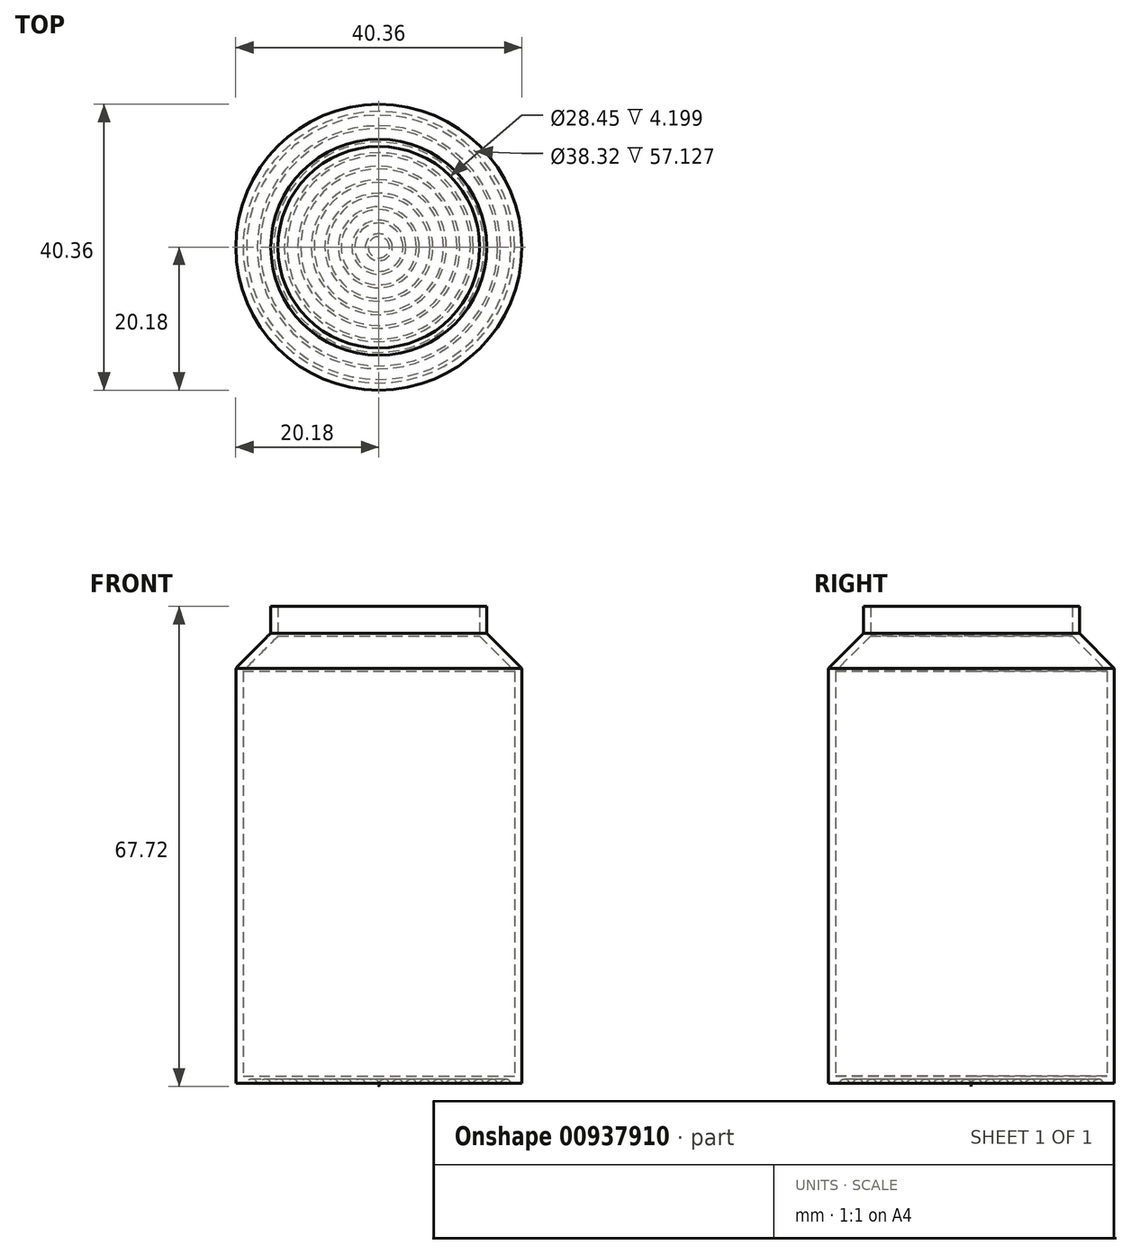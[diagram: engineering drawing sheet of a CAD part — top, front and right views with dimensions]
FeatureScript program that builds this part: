
annotation { "Feature Type Name" : "Feature", "Feature Type Description" : "" }
export const myFeature = defineFeature(function(context is Context, id is Id, definition is map)
    precondition{}
    {
        {
            var Q0;
            Q0=qCreatedBy(makeId("Front.planeOp"),FACE);
            var sketch = newSketch(context, id + "F0", { "sketchPlane" : qUnion([Q0])});
            skLineSegment(sketch, "E0", {"start": v(0, 0) * mm, "end": v(0, 99.8) * mm});
            skLineSegment(sketch, "E1", {"start": v(15.24, 0) * mm, "end": v(14.84, 0) * mm});
            skLineSegment(sketch, "E2", {"start": v(15.24, 67.3) * mm, "end": v(15.24, 63.52) * mm});
            skLineSegment(sketch, "E3", {"start": v(15.24, 63.52) * mm, "end": v(20.18, 58.56) * mm});
            skLineSegment(sketch, "E4", {"start": v(20.18, 58.56) * mm, "end": v(20.18, 0) * mm});
            skLineSegment(sketch, "E5", {"start": v(20.18, 0) * mm, "end": v(18.65, 0) * mm});
            skLineSegment(sketch, "E6.0", {"start": v(15.24, 1.02) * mm, "end": v(0, 1.02) * mm});
            skLineSegment(sketch, "E6.1", {"start": v(14.22, 67.3) * mm, "end": v(14.22, 63.1) * mm});
            skLineSegment(sketch, "E6.2", {"start": v(14.22, 63.1) * mm, "end": v(19.16, 58.14) * mm});
            skLineSegment(sketch, "E6.3", {"start": v(19.16, 58.14) * mm, "end": v(19.16, 1.02) * mm});
            skLineSegment(sketch, "E6.4", {"start": v(19.16, 1.02) * mm, "end": v(15.24, 1.02) * mm});
            skLineSegment(sketch, "E7", {"start": v(14.22, 67.3) * mm, "end": v(15.24, 67.3) * mm});
            skArc(sketch, "E8", {"start": v(1.5, 0) * mm, "mid": v(0.75, 0.57) * mm, "end": v(0, 0) * mm});
            skArc(sketch, "E9.1.0.0", {"start": v(3.4, 0) * mm, "mid": v(2.66, 0.57) * mm, "end": v(1.9, 0) * mm});
            skArc(sketch, "E9.2.0.0", {"start": v(5.31, 0) * mm, "mid": v(4.56, 0.57) * mm, "end": v(3.81, 0) * mm});
            skArc(sketch, "E9.3.0.0", {"start": v(7.22, 0) * mm, "mid": v(6.47, 0.57) * mm, "end": v(5.71, 0) * mm});
            skArc(sketch, "E9.4.0.0", {"start": v(9.12, 0) * mm, "mid": v(8.37, 0.57) * mm, "end": v(7.62, 0) * mm});
            skArc(sketch, "E9.5.0.0", {"start": v(11.03, 0) * mm, "mid": v(10.28, 0.57) * mm, "end": v(9.53, 0) * mm});
            skArc(sketch, "E9.6.0.0", {"start": v(12.93, 0) * mm, "mid": v(12.18, 0.57) * mm, "end": v(11.43, 0) * mm});
            skArc(sketch, "E9.7.0.0", {"start": v(14.84, 0) * mm, "mid": v(14.09, 0.57) * mm, "end": v(13.33, 0) * mm});
            skArc(sketch, "E9.8.0.0", {"start": v(16.74, 0) * mm, "mid": v(16, 0.57) * mm, "end": v(15.24, 0) * mm});
            skArc(sketch, "E9.9.0.0", {"start": v(18.65, 0) * mm, "mid": v(17.9, 0.57) * mm, "end": v(17.14, 0) * mm});
            skLineSegment(sketch, "E9.direction1", {"start": v(1.5, 0) * mm, "end": v(1.9, 0) * mm, "construction": true});
            skLineSegment(sketch, "E10.trimOffspring", {"start": v(5.71, 0) * mm, "end": v(5.31, 0) * mm});
            skLineSegment(sketch, "E11.trimOffspring", {"start": v(3.81, 0) * mm, "end": v(3.4, 0) * mm});
            skLineSegment(sketch, "E12.trimOffspring", {"start": v(1.9, 0) * mm, "end": v(1.5, 0) * mm});
            skLineSegment(sketch, "E13.trimOffspring", {"start": v(7.62, 0) * mm, "end": v(7.22, 0) * mm});
            skLineSegment(sketch, "E14.trimOffspring", {"start": v(11.43, 0) * mm, "end": v(11.03, 0) * mm});
            skLineSegment(sketch, "E15.trimOffspring", {"start": v(9.53, 0) * mm, "end": v(9.12, 0) * mm});
            skLineSegment(sketch, "E16.trimOffspring", {"start": v(13.33, 0) * mm, "end": v(12.93, 0) * mm});
            skLineSegment(sketch, "E17.trimOffspring", {"start": v(17.14, 0) * mm, "end": v(16.74, 0) * mm});
            skSolve(sketch);
        }
        {
            var Q0;
            Q0=makeQuery(id+"F0.imprint","IMPRINT",FACE,{"disambiguationData":[TD([[makeQuery(id+"F0.imprint","IMPRINT",EDGE,{"derivedFrom":sQuery(id+"F0.wireOp",EDGE,"E1")}),-1.0]])]});
            var Q1;
            Q1=sQuery(id+"F0.wireOp",EDGE,"E0");
            revolve(context, id + "F1", {"surfaceOperationType" : NewSurfaceOperationType.NEW, "entities" : qUnion([Q0]), "axis" : qUnion([Q1]), "revolveType" : RevolveType.FULL});
        }
    });
